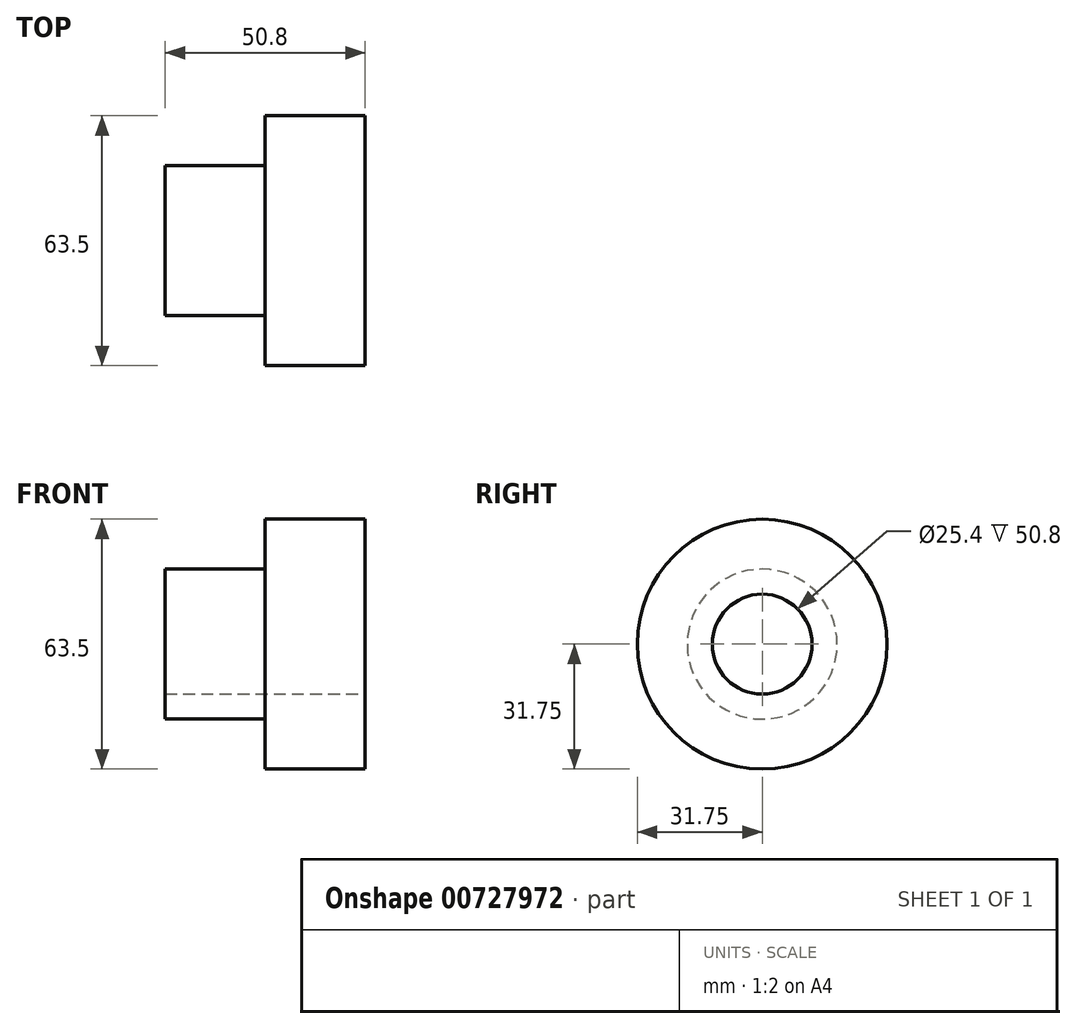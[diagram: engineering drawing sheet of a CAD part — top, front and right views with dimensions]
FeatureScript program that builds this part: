
annotation { "Feature Type Name" : "Feature", "Feature Type Description" : "" }
export const myFeature = defineFeature(function(context is Context, id is Id, definition is map)
    precondition{}
    {
        {
            var Q0;
            Q0=qCreatedBy(makeId("Right.planeOp"),FACE);
            var sketch = newSketch(context, id + "F0", { "sketchPlane" : qUnion([Q0])});
            skCircle(sketch, "E0", {"center": v(0, 0) * mm, "radius": 31.74 * mm});
            skCircle(sketch, "E1", {"center": v(0, 0) * mm, "radius": 19.05 * mm});
            skCircle(sketch, "E2", {"center": v(0, 0) * mm, "radius": 12.7 * mm});
            skSolve(sketch);
        }
        {
            var Q0;
            Q0=makeQuery(id+"F0.imprint","IMPRINT",FACE,{"disambiguationData":[TD([[makeQuery(id+"F0.imprint","IMPRINT",EDGE,{"derivedFrom":sQuery(id+"F0.wireOp",EDGE,"E1")}),1.0]])]});
            extrude(context, id + "F1", {"entities" : qUnion([Q0]), "oppositeDirection" : true, "depth" : 25.4 * mm, "offsetDistance" : 25.4 * mm});
        }
        {
            var Q0;
            Q0=qCreatedBy(makeId("Right.planeOp"),FACE);
            var sketch = newSketch(context, id + "F2", { "sketchPlane" : qUnion([Q0])});
            skCircle(sketch, "E3", {"center": v(0, 0) * mm, "radius": 31.75 * mm});
            skSolve(sketch);
        }
        {
            var Q0;
            Q0=makeQuery(id+"F2.imprint","IMPRINT",FACE,{"disambiguationData":[TD([[makeQuery(id+"F2.imprint","IMPRINT",EDGE,{"derivedFrom":sQuery(id+"F2.wireOp",EDGE,"E3")}),1.0]])]});
            extrude(context, id + "F3", {"entities" : qUnion([Q0]), "operationType" : NewBodyOperationType.ADD, "depth" : 25.4 * mm, "offsetDistance" : 25.4 * mm});
        }
        {
            var Q0;
            Q0=makeQuery(id+"F3.boolean.opBoolean","SPLIT",FACE,{"disambiguationData":[TD([makeQuery(id+"F1.opExtrude","SWEPT_FACE",FACE,{"disambiguationData":[OSD([sQuery(id+"F0.wireOp",EDGE,"E2")])]})])],"derivedFrom":makeQuery(id+"F3.opExtrude","CAP_FACE",FACE,{"disambiguationData":[OSD([sQuery(id+"F2.wireOp",EDGE,"E3")])],"isStart":true})});
            extrude(context, id + "F4", {"entities" : qUnion([Q0]), "operationType" : NewBodyOperationType.REMOVE, "oppositeDirection" : true, "depth" : 25.4 * mm, "offsetDistance" : 25.4 * mm});
        }
    });
